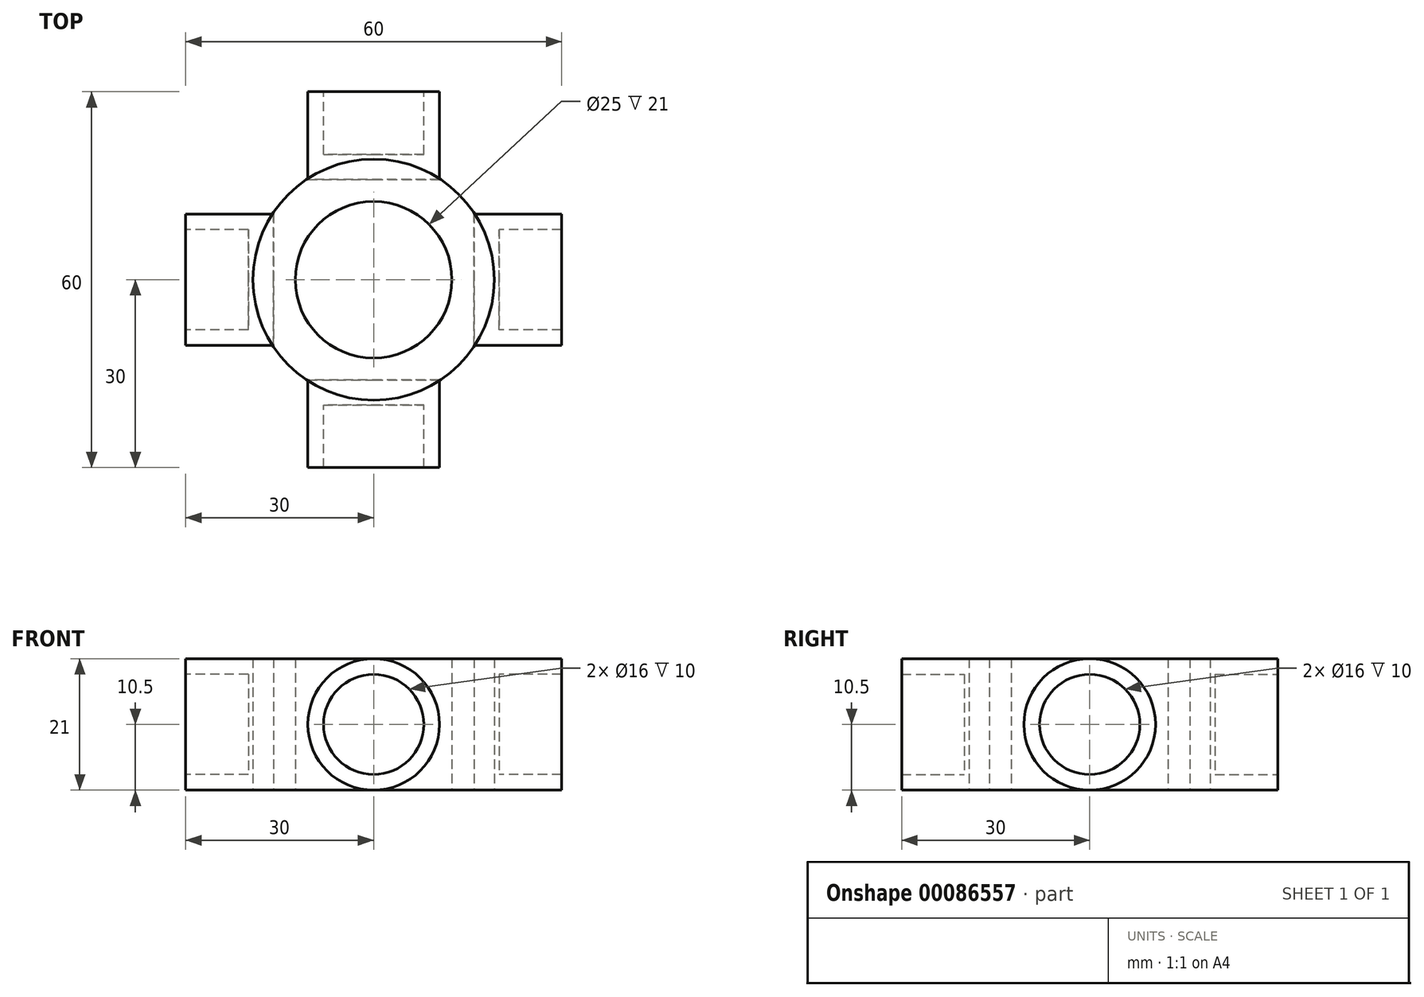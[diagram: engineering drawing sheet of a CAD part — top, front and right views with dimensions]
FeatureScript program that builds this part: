
annotation { "Feature Type Name" : "Feature", "Feature Type Description" : "" }
export const myFeature = defineFeature(function(context is Context, id is Id, definition is map)
    precondition{}
    {
        {
            var Q0;
            Q0=qCreatedBy(makeId("Front.planeOp"),FACE);
            var sketch = newSketch(context, id + "F0", { "sketchPlane" : qUnion([Q0])});
            skLineSegment(sketch, "E0", {"start": v(-17.5, 0) * mm, "end": v(-30, 0) * mm});
            skLineSegment(sketch, "E1", {"start": v(-30, 0) * mm, "end": v(-30, 2.5) * mm});
            skLineSegment(sketch, "E2", {"start": v(-30, 2.5) * mm, "end": v(-20, 2.5) * mm});
            skLineSegment(sketch, "E3", {"start": v(-20, 2.5) * mm, "end": v(-20, 10.5) * mm});
            skLineSegment(sketch, "E4", {"start": v(-20, 10.5) * mm, "end": v(-17.5, 10.5) * mm});
            skLineSegment(sketch, "E5.MirrorCS", {"start": v(20, 10.5) * mm, "end": v(17.5, 10.5) * mm});
            skLineSegment(sketch, "E6.MirrorCS", {"start": v(30, 0) * mm, "end": v(30, 2.5) * mm});
            skLineSegment(sketch, "E7.MirrorCS", {"start": v(17.5, 0) * mm, "end": v(30, 0) * mm});
            skLineSegment(sketch, "E8.MirrorCS", {"start": v(30, 2.5) * mm, "end": v(20, 2.5) * mm});
            skLineSegment(sketch, "E9.MirrorCS", {"start": v(20, 2.5) * mm, "end": v(20, 10.5) * mm});
            skLineSegment(sketch, "E10", {"start": v(-17.5, 10.5) * mm, "end": v(-16, 10.5) * mm});
            skLineSegment(sketch, "E11", {"start": v(-16, 10.5) * mm, "end": v(-16, 0) * mm});
            skLineSegment(sketch, "E12", {"start": v(-16, 0) * mm, "end": v(-17.5, 0) * mm});
            skLineSegment(sketch, "E13", {"start": v(17.5, 10.5) * mm, "end": v(16, 10.5) * mm});
            skLineSegment(sketch, "E14", {"start": v(16, 10.5) * mm, "end": v(16, 0) * mm});
            skLineSegment(sketch, "E15", {"start": v(16, 0) * mm, "end": v(17.5, 0) * mm});
            skSolve(sketch);
        }
        {
            var Q0;
            Q0=makeQuery(id+"F0.imprint","IMPRINT",FACE,{"disambiguationData":[TD([[makeQuery(id+"F0.imprint","IMPRINT",EDGE,{"derivedFrom":sQuery(id+"F0.wireOp",EDGE,"E0")}),-1.0]])]});
            var Q1;
            Q1=makeQuery(id+"F0.imprint","IMPRINT",FACE,{"disambiguationData":[TD([[makeQuery(id+"F0.imprint","IMPRINT",EDGE,{"derivedFrom":sQuery(id+"F0.wireOp",EDGE,"E5.MirrorCS")}),1.0]])]});
            var Q2;
            Q2=sQuery(id+"F0.wireOp",EDGE,"E4");
            revolve(context, id + "F1", {"entities" : qUnion([Q0, Q1]), "axis" : qUnion([Q2]), "revolveType" : RevolveType.FULL});
        }
        {
            var Q0;
            Q0=qCreatedBy(makeId("Right.planeOp"),FACE);
            var sketch = newSketch(context, id + "F2", { "sketchPlane" : qUnion([Q0])});
            skLineSegment(sketch, "E16", {"start": v(-17.5, 0) * mm, "end": v(-30, 0) * mm});
            skLineSegment(sketch, "E17", {"start": v(-30, 0) * mm, "end": v(-30, 2.5) * mm});
            skLineSegment(sketch, "E18", {"start": v(-30, 2.5) * mm, "end": v(-20, 2.5) * mm});
            skLineSegment(sketch, "E19", {"start": v(-20, 2.5) * mm, "end": v(-20, 10.5) * mm});
            skLineSegment(sketch, "E20", {"start": v(-20, 10.5) * mm, "end": v(-17.5, 10.5) * mm});
            skLineSegment(sketch, "E21.MirrorCS", {"start": v(20, 10.5) * mm, "end": v(17.5, 10.5) * mm});
            skLineSegment(sketch, "E22.MirrorCS", {"start": v(17.5, 0) * mm, "end": v(30, 0) * mm});
            skLineSegment(sketch, "E23.MirrorCS", {"start": v(30, 0) * mm, "end": v(30, 2.5) * mm});
            skLineSegment(sketch, "E24.MirrorCS", {"start": v(30, 2.5) * mm, "end": v(20, 2.5) * mm});
            skLineSegment(sketch, "E25.MirrorCS", {"start": v(20, 2.5) * mm, "end": v(20, 10.5) * mm});
            skLineSegment(sketch, "E26", {"start": v(-17.5, 10.5) * mm, "end": v(-16, 10.5) * mm});
            skLineSegment(sketch, "E27", {"start": v(-16, 10.5) * mm, "end": v(-16, 0) * mm});
            skLineSegment(sketch, "E28", {"start": v(-16, 0) * mm, "end": v(-17.5, 0) * mm});
            skLineSegment(sketch, "E29", {"start": v(17.5, 10.5) * mm, "end": v(16, 10.5) * mm});
            skLineSegment(sketch, "E30", {"start": v(16, 10.5) * mm, "end": v(16, 0) * mm});
            skLineSegment(sketch, "E31", {"start": v(16, 0) * mm, "end": v(17.5, 0) * mm});
            skSolve(sketch);
        }
        {
            var Q0;
            Q0 = qSketchRegion(id + "F2", true);
            var Q1;
            Q1=sQuery(id+"F2.wireOp",EDGE,"E21.MirrorCS");
            revolve(context, id + "F3", {"entities" : qUnion([Q0]), "axis" : qUnion([Q1]), "revolveType" : RevolveType.FULL});
        }
        {
            var Q0;
            Q0=qCreatedBy(makeId("Top.planeOp"),FACE);
            var sketch = newSketch(context, id + "F4", { "sketchPlane" : qUnion([Q0])});
            skCircle(sketch, "E32", {"center": v(0, 0) * mm, "radius": 19.25 * mm});
            skSolve(sketch);
        }
        {
            var Q0;
            Q0=makeQuery(id+"F4.imprint","IMPRINT",FACE,{"disambiguationData":[TD([[makeQuery(id+"F4.imprint","IMPRINT",EDGE,{"derivedFrom":sQuery(id+"F4.wireOp",EDGE,"E32")}),1.0]])]});
            extrude(context, id + "F5", {"entities" : qUnion([Q0]), "depth" : 21 * mm});
        }
        {
            var Q0;
            Q0=qCreatedBy(makeId("Top.planeOp"),FACE);
            var sketch = newSketch(context, id + "F6", { "sketchPlane" : qUnion([Q0])});
            skCircle(sketch, "E33", {"center": v(0, 0) * mm, "radius": 14 * mm});
            skSolve(sketch);
        }
        {
            var Q0;
            Q0=sQuery(id+"F6.wireOp",VERTEX,"E33.center");
            var Q1;
            Q1=makeQuery(id+"F5.opExtrude","SWEPT_BODY",BODY,{"disambiguationData":[OSD([sQuery(id+"F4.wireOp",EDGE,"E32")])]});
            hole(context, id + "F7", {"style" : HoleStyle.SIMPLE, "endStyle" : HoleEndStyle.THROUGH, "oppositeDirection" : true, "holeDiameter" : 25 * mm, "locations" : qUnion([Q0]), "scope" : qUnion([Q1]), "isTappedThrough" : true});
        }
    });
